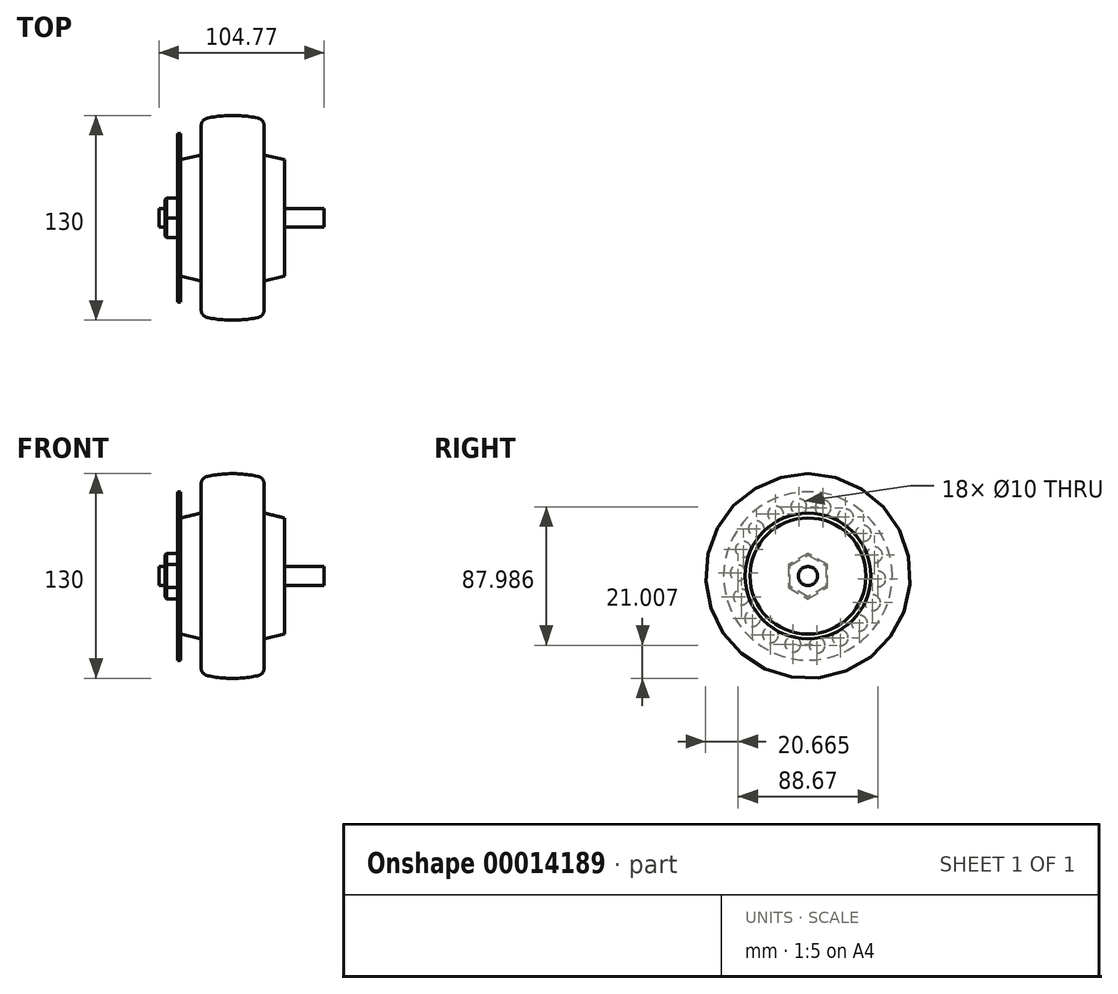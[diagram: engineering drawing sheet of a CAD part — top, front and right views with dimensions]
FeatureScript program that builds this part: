
annotation { "Feature Type Name" : "Feature", "Feature Type Description" : "" }
export const myFeature = defineFeature(function(context is Context, id is Id, definition is map)
    precondition{}
    {
        {
            var Q0;
            Q0=qCreatedBy(makeId("Top.planeOp"),FACE);
            var sketch = newSketch(context, id + "F0", { "sketchPlane" : qUnion([Q0])});
            skLineSegment(sketch, "E0.left", {"start": v(-23.85, 40) * mm, "end": v(-23.85, 58.45) * mm});
            skLineSegment(sketch, "E0.right", {"start": v(16.15, 40) * mm, "end": v(16.15, 58.45) * mm});
            skLineSegment(sketch, "E1.right", {"start": v(-36.85, 0) * mm, "end": v(-36.85, 36.84) * mm});
            skLineSegment(sketch, "E2.MirrorCS", {"start": v(29.15, 0) * mm, "end": v(29.15, 36.84) * mm});
            skLineSegment(sketch, "E3", {"start": v(-23.85, 40) * mm, "end": v(-36.85, 36.84) * mm});
            skLineSegment(sketch, "E4.MirrorCS", {"start": v(16.15, 40) * mm, "end": v(29.15, 36.84) * mm});
            skPoint(sketch, "E5.MirrorCS.end.orphan", {"position": v(29.15, 0) * mm});
            skArc(sketch, "E6", {"start": v(12.18, 63.34) * mm, "mid": v(-3.85, 65) * mm, "end": v(-19.87, 63.34) * mm});
            skArc(sketch, "E7.filletArc", {"start": v(-19.87, 63.34) * mm, "mid": v(-22.73, 61.6) * mm, "end": v(-23.85, 58.45) * mm});
            skArc(sketch, "E8.filletArc", {"start": v(16.15, 58.45) * mm, "mid": v(15.03, 61.6) * mm, "end": v(12.18, 63.34) * mm});
            skLineSegment(sketch, "E9", {"start": v(-36.85, 0) * mm, "end": v(29.15, 0) * mm});
            skSolve(sketch);
        }
        {
            var Q0;
            Q0 = qSketchRegion(id + "F0", true);
            var Q1;
            Q1=sQuery(id+"F0.wireOp",EDGE,"E9");
            revolve(context, id + "F1", {"entities" : qUnion([Q0]), "axis" : qUnion([Q1]), "revolveType" : RevolveType.FULL});
        }
        {
            var Q0;
            Q0=makeQuery(id+"F1.opRevolve","SWEPT_FACE",FACE,{"disambiguationData":[OSD([sQuery(id+"F0.wireOp",EDGE,"E2.MirrorCS")])]});
            var sketch = newSketch(context, id + "F2", { "sketchPlane" : qUnion([Q0])});
            skCircle(sketch, "E10", {"center": v(0, 0) * mm, "radius": 6 * mm});
            skSolve(sketch);
        }
        {
            var Q0;
            Q0 = qSketchRegion(id + "F2", true);
            extrude(context, id + "F3", {"entities" : qUnion([Q0]), "operationType" : NewBodyOperationType.ADD, "depth" : 25 * mm, "hasSecondDirection" : true, "secondDirectionOppositeDirection" : true, "secondDirectionDepth" : 79.77 * mm});
        }
        {
            var Q0;
            Q0=makeQuery(id+"F1.opRevolve","SWEPT_FACE",FACE,{"disambiguationData":[OSD([sQuery(id+"F0.wireOp",EDGE,"E1.right")])]});
            var sketch = newSketch(context, id + "F4", { "sketchPlane" : qUnion([Q0])});
            skCircle(sketch, "E11", {"center": v(0, 0) * mm, "radius": 53.52 * mm});
            skSolve(sketch);
        }
        {
            var Q0;
            Q0 = qSketchRegion(id + "F4", true);
            extrude(context, id + "F5", {"entities" : qUnion([Q0]), "operationType" : NewBodyOperationType.ADD, "depth" : 2 * mm});
        }
        {
            var Q0;
            Q0=makeQuery(id+"F5.opExtrude","CAP_FACE",FACE,{"disambiguationData":[OSD([sQuery(id+"F4.wireOp",EDGE,"E11")])],"isStart":false});
            var sketch = newSketch(context, id + "F6", { "sketchPlane" : qUnion([Q0])});
            skCircle(sketch, "E12", {"center": v(-9.58, 43.33) * mm, "radius": 5 * mm});
            skSolve(sketch);
        }
        {
            var Q0;
            Q0 = qSketchRegion(id + "F6", true);
            extrude(context, id + "F7", {"entities" : qUnion([Q0]), "operationType" : NewBodyOperationType.REMOVE, "endBound" : BoundingType.UP_TO_NEXT, "oppositeDirection" : true, "depth" : 25 * mm});
        }
        {
            var Q0;
            Q0=makeQuery(id+"F7.boolean.opBoolean","COPY",FACE,{"derivedFrom":makeQuery(id+"F7.opExtrude","SWEPT_FACE",FACE,{"disambiguationData":[OSD([sQuery(id+"F6.wireOp",EDGE,"E12")])]})});
            var Q1;
            {var subQ0=sQuery(id+"F2.wireOp",EDGE,"E10");Q1=makeQuery(id+"F3.boolean.opBoolean","SPLIT",FACE,{"disambiguationData":[TD([makeQuery(id+"F1.opRevolve","SWEPT_FACE",FACE,{"disambiguationData":[OSD([sQuery(id+"F0.wireOp",EDGE,"E1.right")])]})])],"derivedFrom":makeQuery(id+"F3.opExtrude","SWEPT_FACE",FACE,{"disambiguationData":[OSD([subQ0])]})});}
            circularPattern(context, id + "F8", {"faces" : qUnion([Q0]), "axis" : qUnion([Q1]), "angle" : 20 * degree, "instanceCount" : 18, "patternType" : PatternType.FACE});
        }
        {
            var Q0;
            Q0=makeQuery(id+"F5.opExtrude","CAP_FACE",FACE,{"disambiguationData":[OSD([sQuery(id+"F4.wireOp",EDGE,"E11")])],"isStart":false});
            var sketch = newSketch(context, id + "F9", { "sketchPlane" : qUnion([Q0])});
            skCircle(sketch, "E13.cCircle", {"center": v(0, 0) * mm, "radius": 12.5 * mm, "construction": true});
            skLineSegment(sketch, "E13.0", {"start": v(12.5, 7.22) * mm, "end": v(12.5, -7.22) * mm});
            skLineSegment(sketch, "E13.1", {"start": v(12.5, -7.22) * mm, "end": v(0, -14.43) * mm});
            skLineSegment(sketch, "E13.2", {"start": v(0, -14.43) * mm, "end": v(-12.5, -7.22) * mm});
            skLineSegment(sketch, "E13.3", {"start": v(-12.5, -7.22) * mm, "end": v(-12.5, 7.22) * mm});
            skLineSegment(sketch, "E13.4", {"start": v(-12.5, 7.22) * mm, "end": v(0, 14.43) * mm});
            skLineSegment(sketch, "E13.5", {"start": v(0, 14.43) * mm, "end": v(12.5, 7.22) * mm});
            skPoint(sketch, "E13.0.midPoint", {"position": v(12.5, 0) * mm});
            skSolve(sketch);
        }
        {
            var Q0;
            Q0 = qSketchRegion(id + "F9", true);
            extrude(context, id + "F10", {"entities" : qUnion([Q0]), "operationType" : NewBodyOperationType.ADD, "depth" : 8 * mm});
        }
        {
            var Q0;
            Q0=makeQuery(id+"F10.opExtrude","CAP_EDGE",EDGE,{"disambiguationData":[OSD([sQuery(id+"F9.wireOp",EDGE,"E13.3")])],"isStart":false});
            var Q1;
            Q1=makeQuery(id+"F10.opExtrude","CAP_EDGE",EDGE,{"disambiguationData":[OSD([sQuery(id+"F9.wireOp",EDGE,"E13.4")])],"isStart":false});
            var Q2;
            Q2=makeQuery(id+"F10.opExtrude","CAP_EDGE",EDGE,{"disambiguationData":[OSD([sQuery(id+"F9.wireOp",EDGE,"E13.5")])],"isStart":false});
            var Q3;
            Q3=makeQuery(id+"F10.opExtrude","CAP_EDGE",EDGE,{"disambiguationData":[OSD([sQuery(id+"F9.wireOp",EDGE,"E13.0")])],"isStart":false});
            var Q4;
            Q4=makeQuery(id+"F10.opExtrude","CAP_EDGE",EDGE,{"disambiguationData":[OSD([sQuery(id+"F9.wireOp",EDGE,"E13.1")])],"isStart":false});
            var Q5;
            Q5=makeQuery(id+"F10.opExtrude","CAP_EDGE",EDGE,{"disambiguationData":[OSD([sQuery(id+"F9.wireOp",EDGE,"E13.2")])],"isStart":false});
            chamfer(context, id + "F11", {"entities" : qUnion([Q0, Q1, Q2, Q3, Q4, Q5]), "width" : 1 * mm, "tangentPropagation" : true});
        }
    });
